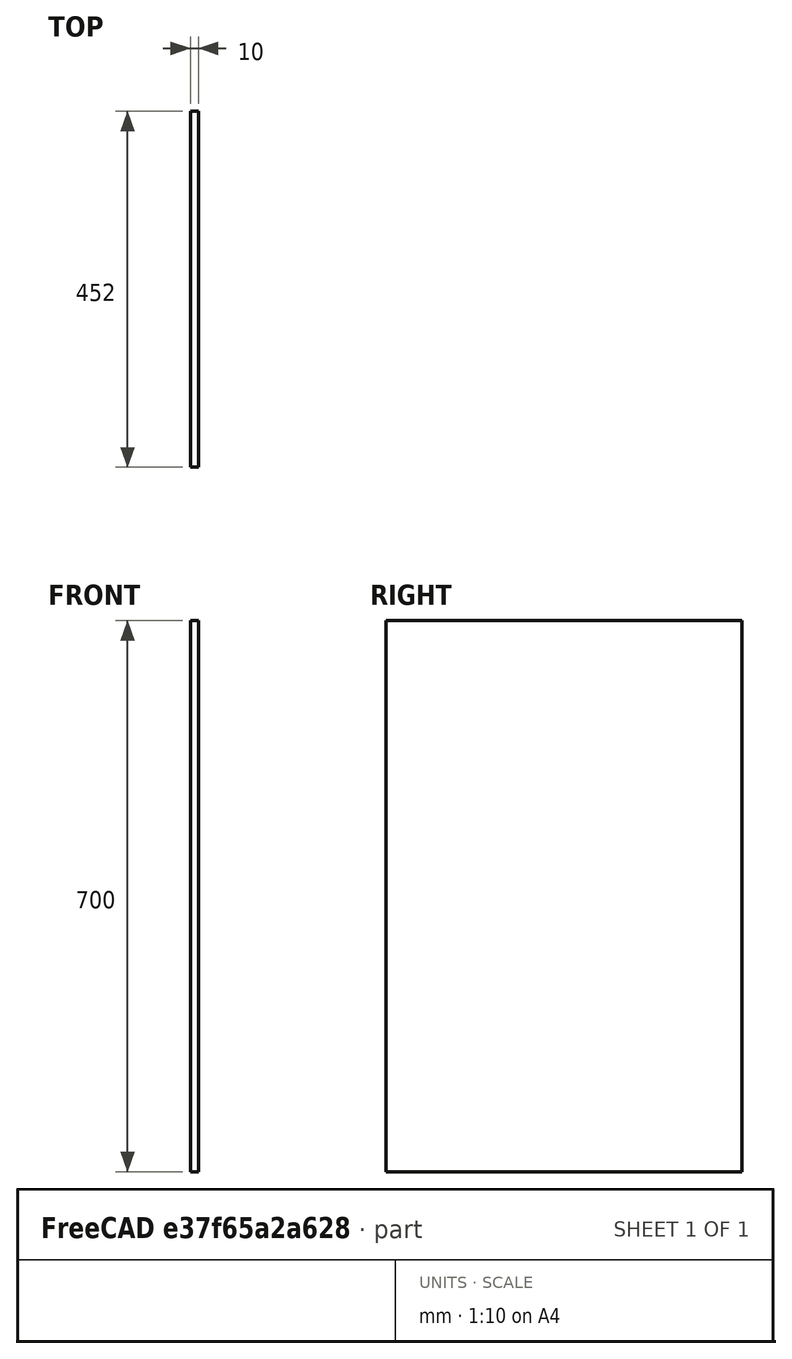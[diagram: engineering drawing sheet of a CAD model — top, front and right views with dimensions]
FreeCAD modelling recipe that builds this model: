
FCSTD DOCUMENT  (FreeCAD 0.18R16131 (Git))
Label: 500_Front_YZ_1
License: All rights reserved
LicenseURL: http://en.wikipedia.org/wiki/All_rights_reserved
objects: Sketcher::SketchObject×1, Spreadsheet::Sheet×1, PartDesign::Pad×1, PartDesign::Body×1
note: 4 computed .brp shape members not serialized (recipe doc carries the construction recipe); baked Part::Feature solids carry a one-line shape summary decoded from their .brp

FEATURE [Sketcher::SketchObject] Sketch
  MapMode = 4
  Placement = pos=(0,0,0) rot=(0.57735,0.57735,0.57735;2.0944rad)
  Support = -> [XY_Plane]
  expr: Constraints[6] = Spreadsheet.nY
  expr: Constraints[5] = Spreadsheet.nZ
  sketch-geometry (5):
    g0: LineSegment StartX=0 StartY=0 StartZ=0 EndX=0 EndY=700 EndZ=0
    g1: LineSegment StartX=452 StartY=0 StartZ=0 EndX=452 EndY=700 EndZ=0
    g2: LineSegment StartX=452 StartY=700 StartZ=0 EndX=0 EndY=700 EndZ=0
    g3: LineSegment StartX=226 StartY=0 StartZ=0 EndX=0 EndY=0 EndZ=0
    g4: LineSegment StartX=452 StartY=0 StartZ=0 EndX=226 EndY=0 EndZ=0
  constraints (14):
    c: Vertical(g0)
    c: Vertical(g1)
    c: Coincident(g2,g1)
    c: Coincident(g2,g0)
    c: Horizontal(g2)
    c: DistanceY(g1,g1) = 700
    c: DistanceX(g2,g2) = 452
    c: Coincident(g3,g0)
    c: Coincident(g4,g1)
    c: Horizontal(g4)
    c: Equal(g3,g4)
    c: Coincident(g4,g3)
    c: Horizontal(g3)
    c: Coincident(g0,g-1)
FEATURE [Spreadsheet::Sheet] Spreadsheet  label="xls"
  cells = B7=KEYBOARD FRONT; B8=Width; C8=nY; D8(nY)==500 - 19 - 19 - 10; B9=Height; C9=nZ; D9(nZ)=700; E9=F(T); B10=Thickness; C10=nT; D10(nT)=10
FEATURE [PartDesign::Pad] Pad
  Length = 10
  Length2 = 100
  Profile = -> Sketch
  Reversed = true
  Type = 0
  expr: Length = Spreadsheet.nT
FEATURE [PartDesign::Body] Body
  Group = -> [Sketch,Pad]
  Origin = -> Origin
  Tip = -> Pad
